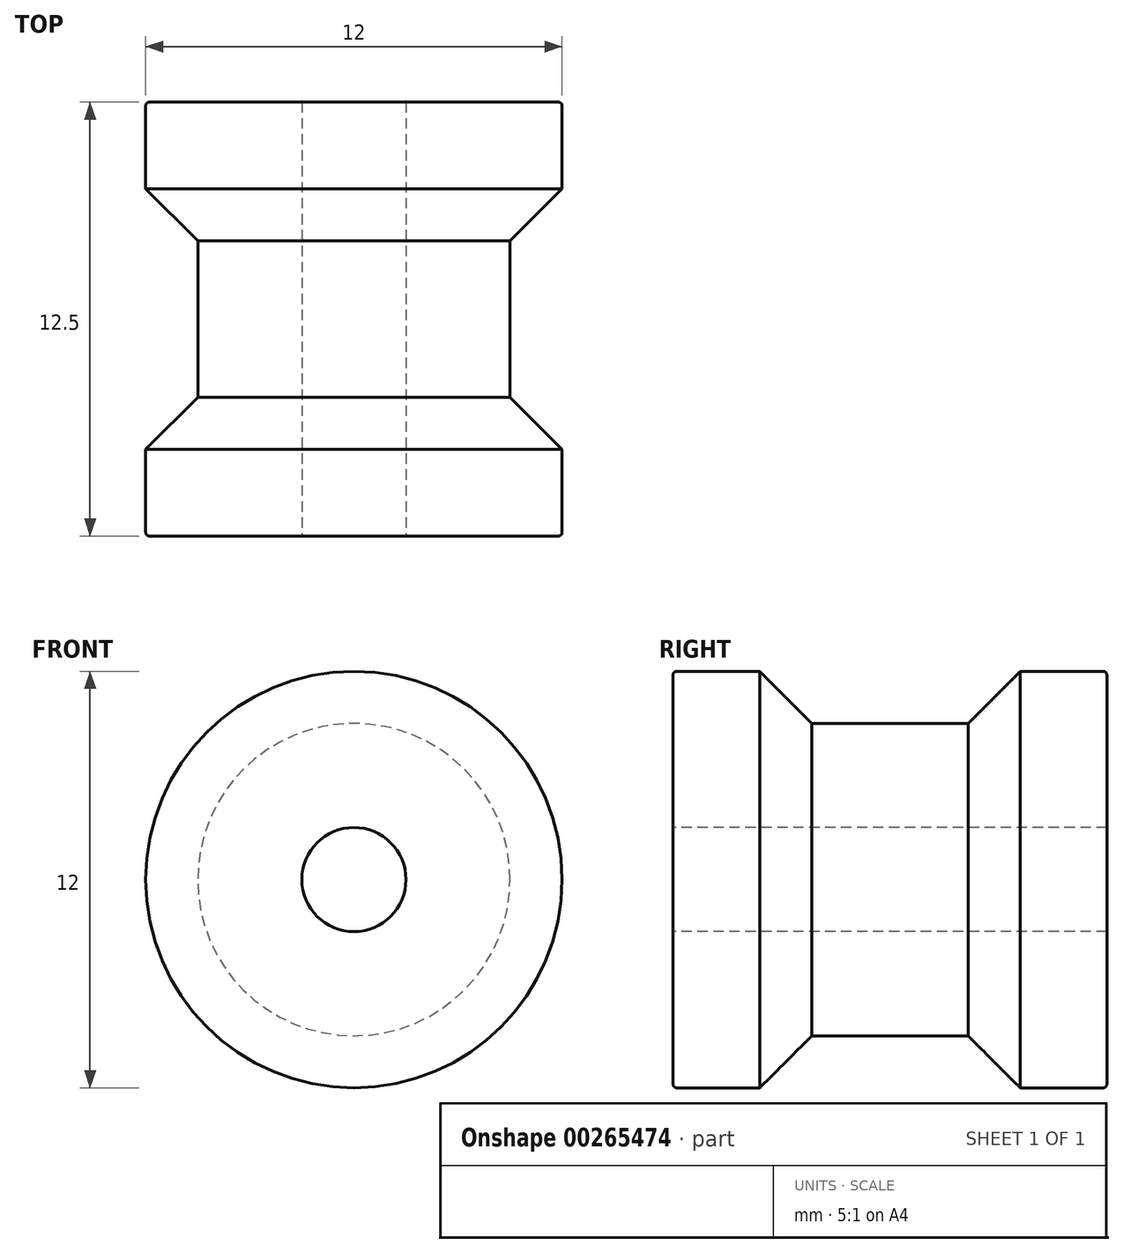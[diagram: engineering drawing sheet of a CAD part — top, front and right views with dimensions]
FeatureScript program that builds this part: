
annotation { "Feature Type Name" : "Feature", "Feature Type Description" : "" }
export const myFeature = defineFeature(function(context is Context, id is Id, definition is map)
    precondition{}
    {
        {
            var Q0;
            Q0=qCreatedBy(makeId("Front.planeOp"),FACE);
            var sketch = newSketch(context, id + "F0", { "sketchPlane" : qUnion([Q0])});
            skCircle(sketch, "E0", {"center": v(0, 0) * mm, "radius": 6 * mm});
            skSolve(sketch);
        }
        {
            var Q0;
            Q0=makeQuery(id+"F0.imprint","IMPRINT",FACE,{"disambiguationData":[TD([[makeQuery(id+"F0.imprint","IMPRINT",EDGE,{"derivedFrom":sQuery(id+"F0.wireOp",EDGE,"E0")}),1.0]])]});
            extrude(context, id + "F1", {"entities" : qUnion([Q0]), "depth" : 4 * mm});
        }
        {
            var Q0;
            Q0=makeQuery(id+"F1.opExtrude","CAP_FACE",FACE,{"disambiguationData":[OSD([sQuery(id+"F0.wireOp",EDGE,"E0")])],"isStart":false});
            var sketch = newSketch(context, id + "F2", { "sketchPlane" : qUnion([Q0])});
            skCircle(sketch, "E1", {"center": v(0, 0) * mm, "radius": 4.5 * mm});
            skSolve(sketch);
        }
        {
            var Q0;
            Q0=makeQuery(id+"F2.imprint","IMPRINT",FACE,{"disambiguationData":[TD([[makeQuery(id+"F2.imprint","IMPRINT",EDGE,{"derivedFrom":sQuery(id+"F2.wireOp",EDGE,"E1")}),1.0]])]});
            extrude(context, id + "F3", {"entities" : qUnion([Q0]), "operationType" : NewBodyOperationType.ADD, "depth" : 4.5 * mm});
        }
        {
            var Q0;
            Q0=makeQuery(id+"F3.opExtrude","CAP_FACE",FACE,{"disambiguationData":[OSD([sQuery(id+"F2.wireOp",EDGE,"E1")])],"isStart":false});
            var sketch = newSketch(context, id + "F4", { "sketchPlane" : qUnion([Q0])});
            skCircle(sketch, "E2", {"center": v(0, 0) * mm, "radius": 6 * mm});
            skSolve(sketch);
        }
        {
            var Q0;
            Q0=makeQuery(id+"F4.imprint","IMPRINT",FACE,{"disambiguationData":[TD([[makeQuery(id+"F4.imprint","IMPRINT",EDGE,{"derivedFrom":sQuery(id+"F4.wireOp",EDGE,"E2")}),1.0]])]});
            var Q1;
            Q1=makeQuery(id+"F4.imprint","IMPRINT",FACE,{"disambiguationData":[TD([[makeQuery(id+"F4.imprint","IMPRINT",EDGE,{"derivedFrom":makeQuery(id+"F3.opExtrude","CAP_EDGE",EDGE,{"disambiguationData":[OSD([sQuery(id+"F2.wireOp",EDGE,"E1")])],"isStart":false})}),1.0]])]});
            extrude(context, id + "F5", {"entities" : qUnion([Q0, Q1]), "operationType" : NewBodyOperationType.ADD, "depth" : 4 * mm});
        }
        {
            var Q0;
            Q0=makeQuery(id+"F5.opExtrude","CAP_FACE",FACE,{"disambiguationData":[OSD([sQuery(id+"F4.wireOp",EDGE,"E2")])],"isStart":false});
            var sketch = newSketch(context, id + "F6", { "sketchPlane" : qUnion([Q0])});
            skCircle(sketch, "E3", {"center": v(0, 0) * mm, "radius": 1.5 * mm});
            skSolve(sketch);
        }
        {
            var Q0;
            Q0=makeQuery(id+"F6.imprint","IMPRINT",FACE,{"disambiguationData":[TD([[makeQuery(id+"F6.imprint","IMPRINT",EDGE,{"derivedFrom":sQuery(id+"F6.wireOp",EDGE,"E3")}),1.0]])]});
            extrude(context, id + "F7", {"entities" : qUnion([Q0]), "operationType" : NewBodyOperationType.REMOVE, "oppositeDirection" : true, "depth" : 15 * mm});
        }
        {
            var Q0;
            Q0=makeQuery(id+"F5.opExtrude","CAP_EDGE",EDGE,{"disambiguationData":[OSD([sQuery(id+"F4.wireOp",EDGE,"E2")])],"isStart":true});
            var Q1;
            Q1=makeQuery(id+"F1.opExtrude","CAP_EDGE",EDGE,{"disambiguationData":[OSD([sQuery(id+"F0.wireOp",EDGE,"E0")])],"isStart":false});
            chamfer(context, id + "F8", {"entities" : qUnion([Q0, Q1]), "width" : 1.5 * mm, "tangentPropagation" : true});
        }
        {
            var Q0;
            Q0=makeQuery(id+"F5.opExtrude","CAP_EDGE",EDGE,{"disambiguationData":[OSD([sQuery(id+"F4.wireOp",EDGE,"E2")])],"isStart":false});
            var Q1;
            Q1=makeQuery(id+"F1.opExtrude","CAP_EDGE",EDGE,{"disambiguationData":[OSD([sQuery(id+"F0.wireOp",EDGE,"E0")])],"isStart":true});
            fillet(context, id + "F9", {"entities" : qUnion([Q0, Q1]), "radius" : 0.1 * mm, "tangentPropagation" : true, "allowEdgeOverflow" : false});
        }
    });
